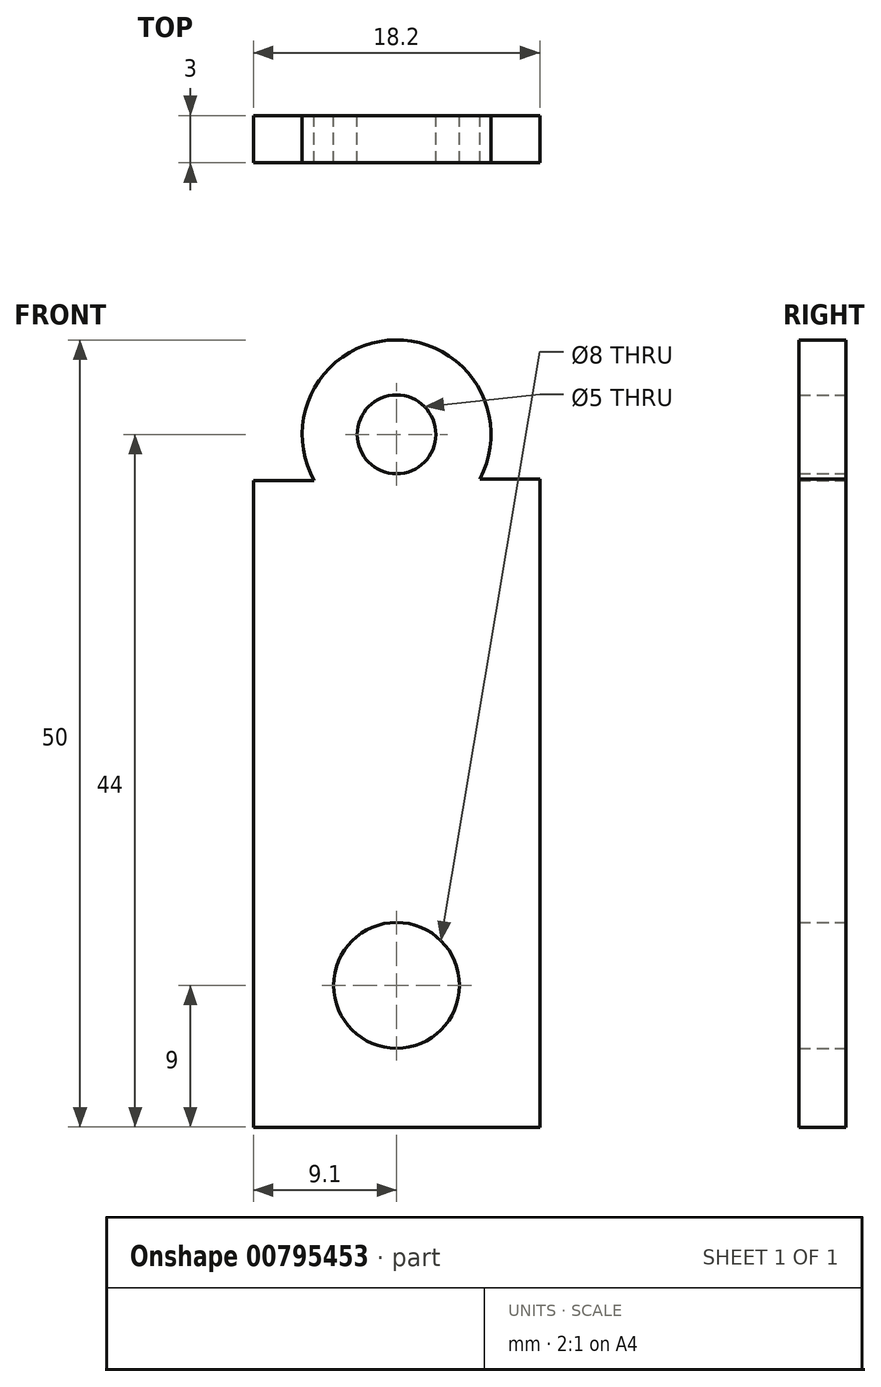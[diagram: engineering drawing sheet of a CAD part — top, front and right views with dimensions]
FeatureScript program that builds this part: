
annotation { "Feature Type Name" : "Feature", "Feature Type Description" : "" }
export const myFeature = defineFeature(function(context is Context, id is Id, definition is map)
    precondition{}
    {
        {
            var Q0;
            Q0=qCreatedBy(makeId("Front.planeOp"),FACE);
            var sketch = newSketch(context, id + "F0", { "sketchPlane" : qUnion([Q0])});
            skLineSegment(sketch, "E0.right", {"start": v(9.1, 15.57) * mm, "end": v(9.1, 15.57) * mm});
            skPoint(sketch, "E0.middle", {"position": v(0, 0) * mm});
            skPoint(sketch, "E1", {"position": v(0, 18.4) * mm});
            skLineSegment(sketch, "E2", {"start": v(-9.1, 12.03) * mm, "end": v(-9.1, -25.6) * mm});
            skLineSegment(sketch, "E3.top", {"start": v(9.1, 15.57) * mm, "end": v(5.3, 15.57) * mm});
            skPoint(sketch, "E4", {"position": v(0, -16.6) * mm});
            skCircle(sketch, "E5", {"center": v(0, -16.6) * mm, "radius": 4 * mm});
            skCircle(sketch, "E6", {"center": v(0, 18.4) * mm, "radius": 2.5 * mm});
            skArc(sketch, "E7", {"start": v(9.1, 15.57) * mm, "mid": v(9.1, 15.57) * mm, "end": v(9.1, 15.57) * mm});
            skArc(sketch, "E8", {"start": v(5.3, 15.57) * mm, "mid": v(-0.06, 24.4) * mm, "end": v(-5.23, 15.46) * mm});
            skLineSegment(sketch, "E9.left", {"start": v(9.1, 15.57) * mm, "end": v(9.1, -25.6) * mm});
            skLineSegment(sketch, "E10", {"start": v(-9.1, -25.6) * mm, "end": v(9.1, -25.6) * mm});
            skLineSegment(sketch, "E11", {"start": v(-5.23, 15.46) * mm, "end": v(-9.1, 15.46) * mm});
            skLineSegment(sketch, "E12", {"start": v(-9.1, 15.46) * mm, "end": v(-9.1, 12.03) * mm});
            skSolve(sketch);
        }
        {
            var Q0;
            Q0=makeQuery(id+"F0.imprint","IMPRINT",FACE,{"disambiguationData":[TD([[makeQuery(id+"F0.imprint","IMPRINT",EDGE,{"derivedFrom":sQuery(id+"F0.wireOp",EDGE,"E5")}),-1.0]])]});
            extrude(context, id + "F1", {"entities" : qUnion([Q0]), "depth" : 3 * mm, "offsetDistance" : 25 * mm});
        }
    });
